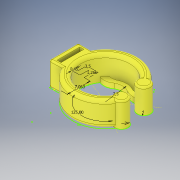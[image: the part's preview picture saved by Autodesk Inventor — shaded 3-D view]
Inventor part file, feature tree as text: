
AUTODESK INVENTOR PART (.ipt)
format: ipt  version: 2019 (Build 230136000, 136)  size: 666,624 bytes
history: native  units: mm
features: fillet x11, extrude x3, sketch x1
ambient origin geometry x8: Origin, YZ Plane, XZ Plane, XY Plane, X Axis, Y Axis, Z Axis, Center Point
bodies: Body1 (feature_tree)
feature tree (15):
  sketch  "Sketch1"  dims[d39=21.816616mm d40=7.5mm d113=10.0mm d114=2.0mm d115=2.0mm d118=0.07854mm d119=7.5mm d120=0.0mm d121=1.5mm d122=0.0mm d123=1.5mm d124=0.0mm d125=1.0mm d126=1.0mm d127=1.0mm d128=0.5mm d129=0.5mm d130=0.5mm d131=0.5mm d132=0.5mm d133=1.0mm d134=1.0mm d135=0.5mm d136=3.5mm d137=7.06251mm d138=1.266mm]
  extrude  "Extrusion8"  Depth=0.5mm
  extrude  "Extrusion9"  Depth=10.0mm
  extrude  "Extrusion10"  Depth=0.5mm
  fillet  "Fillet32"  Radius=2.0mm
  fillet  "Fillet33"  Radius=0.07854mm
  fillet  "Fillet34"  Radius=7.5mm
  fillet  "Fillet35"  Radius=1.5mm
  fillet  "Fillet36"  Radius=1.5mm
  fillet  "Fillet37"  Radius=1.0mm
  fillet  "Fillet38"  Radius=1.0mm
  fillet  "Fillet39"  Radius=1.0mm
  fillet  "Fillet40"  Radius=0.5mm
  fillet  "Fillet41"  Radius=0.5mm
  fillet  "Fillet42"  Radius=0.5mm
